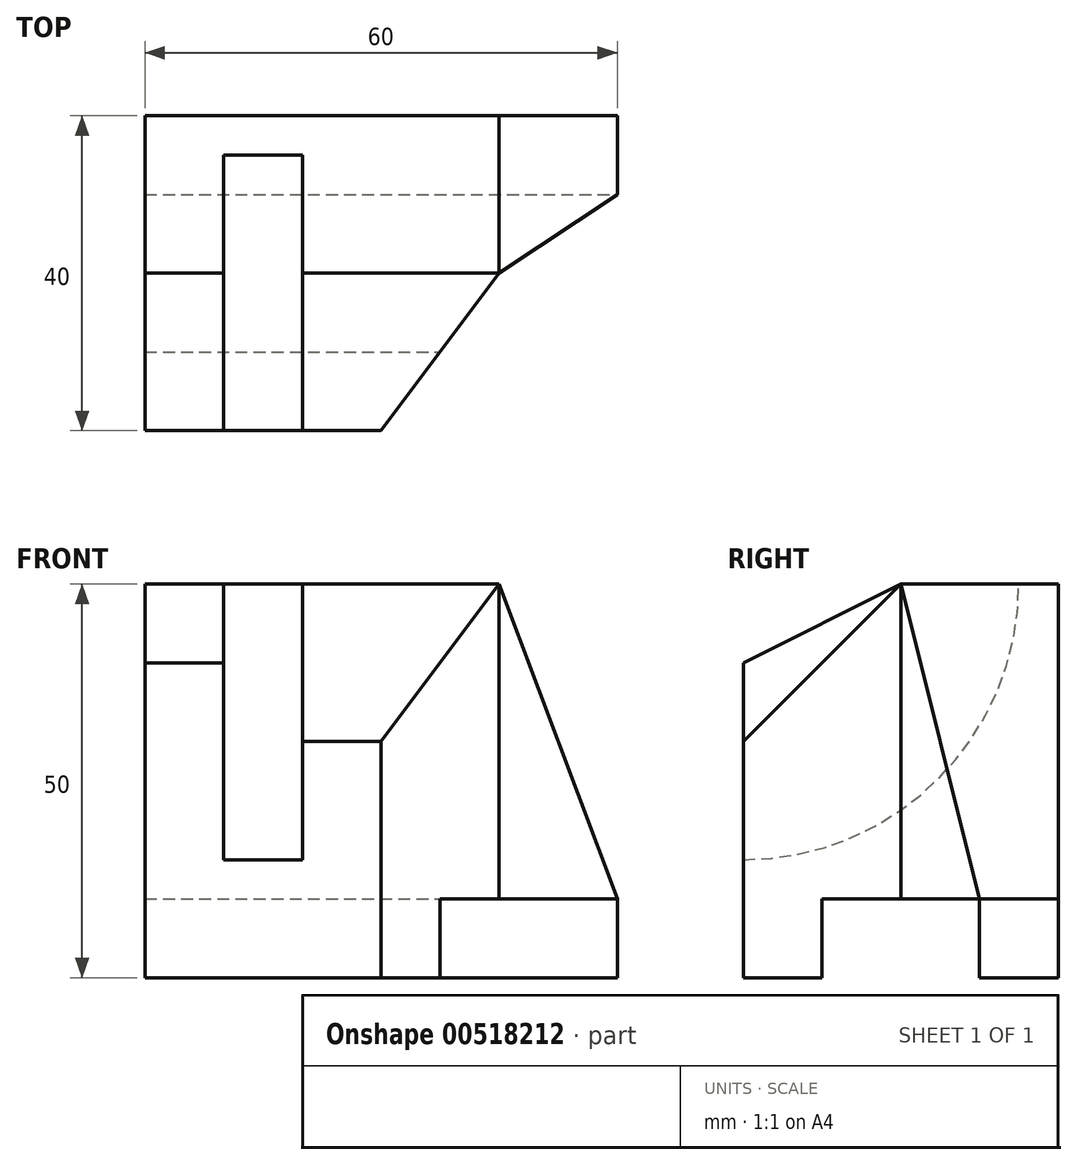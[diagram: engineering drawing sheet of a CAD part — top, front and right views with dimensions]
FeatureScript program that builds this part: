
annotation { "Feature Type Name" : "Feature", "Feature Type Description" : "" }
export const myFeature = defineFeature(function(context is Context, id is Id, definition is map)
    precondition{}
    {
        {
            var Q0;
            Q0=qCreatedBy(makeId("Top.planeOp"),FACE);
            var sketch = newSketch(context, id + "F0", { "sketchPlane" : qUnion([Q0])});
            skLineSegment(sketch, "E0.bottom", {"start": v(0, 0) * mm, "end": v(60, 0) * mm});
            skLineSegment(sketch, "E0.top", {"start": v(0, 40) * mm, "end": v(60, 40) * mm});
            skLineSegment(sketch, "E0.left", {"start": v(0, 0) * mm, "end": v(0, 40) * mm});
            skLineSegment(sketch, "E0.right", {"start": v(60, 0) * mm, "end": v(60, 40) * mm});
            skSolve(sketch);
        }
        {
            var Q0;
            Q0=makeQuery(id+"F0.imprint","IMPRINT",FACE,{"disambiguationData":[TD([[makeQuery(id+"F0.imprint","IMPRINT",EDGE,{"derivedFrom":sQuery(id+"F0.wireOp",EDGE,"E0.bottom")}),1.0]])]});
            extrude(context, id + "F1", {"entities" : qUnion([Q0]), "depth" : 50 * mm, "offsetDistance" : 25 * mm});
        }
        {
            var Q0;
            Q0=makeQuery(id+"F1.opExtrude","CAP_FACE",FACE,{"disambiguationData":[OSD([sQuery(id+"F0.wireOp",EDGE,"E0.bottom"),sQuery(id+"F0.wireOp",EDGE,"E0.top"),sQuery(id+"F0.wireOp",EDGE,"E0.left"),sQuery(id+"F0.wireOp",EDGE,"E0.right")])],"isStart":false});
            var sketch = newSketch(context, id + "F2", { "sketchPlane" : qUnion([Q0])});
            skLineSegment(sketch, "E1", {"start": v(10, 0) * mm, "end": v(10, 35) * mm});
            skLineSegment(sketch, "E2", {"start": v(10, 35) * mm, "end": v(20, 35) * mm});
            skLineSegment(sketch, "E3", {"start": v(20, 35) * mm, "end": v(20, 0) * mm});
            skSolve(sketch);
        }
        {
            var Q0;
            {var subQ0=sQuery(id+"F2.wireOp",EDGE,"E1");Q0=makeQuery(id+"F2.imprint","IMPRINT",FACE,{"disambiguationData":[TD([[makeQuery(id+"F2.imprint","IMPRINT",EDGE,{"derivedFrom":subQ0}),-1.0]])]});}
            extrude(context, id + "F3", {"entities" : qUnion([Q0]), "operationType" : NewBodyOperationType.REMOVE, "oppositeDirection" : true, "depth" : 35 * mm, "offsetDistance" : 25 * mm});
        }
        {
            var Q0;
            Q0=makeQuery(id+"F3.boolean.opBoolean","COPY",EDGE,{"derivedFrom":makeQuery(id+"F3.opExtrude","CAP_EDGE",EDGE,{"disambiguationData":[OSD([sQuery(id+"F2.wireOp",EDGE,"E2")])],"isStart":false})});
            fillet(context, id + "F4", {"entities" : qUnion([Q0]), "radius" : 35 * mm, "tangentPropagation" : true, "allowEdgeOverflow" : false});
        }
        {
            var Q0;
            Q0=makeQuery(id+"F1.opExtrude","SWEPT_FACE",FACE,{"disambiguationData":[OSD([sQuery(id+"F0.wireOp",EDGE,"E0.right")])]});
            var sketch = newSketch(context, id + "F5", { "sketchPlane" : qUnion([Q0])});
            skLineSegment(sketch, "E4", {"start": v(10, 0) * mm, "end": v(10, 10) * mm});
            skLineSegment(sketch, "E5", {"start": v(10, 10) * mm, "end": v(30, 10) * mm});
            skLineSegment(sketch, "E6", {"start": v(30, 10) * mm, "end": v(30, 0) * mm});
            skSolve(sketch);
        }
        {
            var Q0;
            {var subQ0=sQuery(id+"F5.wireOp",EDGE,"E4");Q0=makeQuery(id+"F5.imprint","IMPRINT",FACE,{"disambiguationData":[TD([[makeQuery(id+"F5.imprint","IMPRINT",EDGE,{"derivedFrom":subQ0}),-1.0]])]});}
            extrude(context, id + "F6", {"entities" : qUnion([Q0]), "operationType" : NewBodyOperationType.REMOVE, "endBound" : BoundingType.THROUGH_ALL, "oppositeDirection" : true, "depth" : 25 * mm, "offsetDistance" : 25 * mm});
        }
        {
            var Q0;
            Q0=makeQuery(id+"F1.opExtrude","CAP_FACE",FACE,{"disambiguationData":[OSD([sQuery(id+"F0.wireOp",EDGE,"E0.bottom"),sQuery(id+"F0.wireOp",EDGE,"E0.top"),sQuery(id+"F0.wireOp",EDGE,"E0.left"),sQuery(id+"F0.wireOp",EDGE,"E0.right")])],"isStart":false});
            var sketch = newSketch(context, id + "F7", { "sketchPlane" : qUnion([Q0])});
            skLineSegment(sketch, "E7", {"start": v(60, 20) * mm, "end": v(20, 20) * mm});
            skLineSegment(sketch, "E8", {"start": v(45, 40) * mm, "end": v(45, 20) * mm});
            skLineSegment(sketch, "E9", {"start": v(20, 30) * mm, "end": v(60, 30) * mm});
            skLineSegment(sketch, "E10", {"start": v(60, 30) * mm, "end": v(45, 20) * mm});
            skSolve(sketch);
        }
        {
            var Q0;
            {var subQ3=sQuery(id+"F7.wireOp",EDGE,"E10");Q0=makeQuery(id+"F7.imprint","IMPRINT",FACE,{"disambiguationData":[TD([[makeQuery(id+"F7.imprint","IMPRINT",EDGE,{"derivedFrom":subQ3}),1.0]])]});}
            extrude(context, id + "F8", {"entities" : qUnion([Q0]), "operationType" : NewBodyOperationType.REMOVE, "endBound" : BoundingType.THROUGH_ALL, "oppositeDirection" : true, "depth" : 25 * mm, "offsetDistance" : 25 * mm});
        }
        {
            var Q0;
            Q0=makeQuery(id+"F1.opExtrude","CAP_FACE",FACE,{"disambiguationData":[OSD([sQuery(id+"F0.wireOp",EDGE,"E0.bottom"),sQuery(id+"F0.wireOp",EDGE,"E0.top"),sQuery(id+"F0.wireOp",EDGE,"E0.left"),sQuery(id+"F0.wireOp",EDGE,"E0.right")])],"isStart":false});
            var sketch = newSketch(context, id + "F9", { "sketchPlane" : qUnion([Q0])});
            skLineSegment(sketch, "E11", {"start": v(45, 20) * mm, "end": v(30, 0) * mm});
            skSolve(sketch);
        }
        {
            var Q0;
            {var subQ0=sQuery(id+"F9.wireOp",EDGE,"E11");Q0=makeQuery(id+"F9.imprint","IMPRINT",FACE,{"disambiguationData":[TD([[makeQuery(id+"F9.imprint","IMPRINT",EDGE,{"derivedFrom":subQ0}),1.0]])]});}
            extrude(context, id + "F10", {"entities" : qUnion([Q0]), "operationType" : NewBodyOperationType.REMOVE, "endBound" : BoundingType.THROUGH_ALL, "oppositeDirection" : true, "depth" : 25 * mm, "offsetDistance" : 25 * mm});
        }
        {
            var Q0;
            Q0=makeQuery(id+"F1.opExtrude","CAP_FACE",FACE,{"disambiguationData":[OSD([sQuery(id+"F0.wireOp",EDGE,"E0.bottom"),sQuery(id+"F0.wireOp",EDGE,"E0.top"),sQuery(id+"F0.wireOp",EDGE,"E0.left"),sQuery(id+"F0.wireOp",EDGE,"E0.right")])],"isStart":false});
            var sketch = newSketch(context, id + "F11", { "sketchPlane" : qUnion([Q0])});
            skLineSegment(sketch, "E12", {"start": v(45, 20) * mm, "end": v(45, 40) * mm});
            skSolve(sketch);
        }
        {
            var Q0;
            Q0=makeQuery(id+"F1.opExtrude","SWEPT_FACE",FACE,{"disambiguationData":[OSD([sQuery(id+"F0.wireOp",EDGE,"E0.top")])]});
            var sketch = newSketch(context, id + "F12", { "sketchPlane" : qUnion([Q0])});
            skLineSegment(sketch, "E13", {"start": v(-45, 50) * mm, "end": v(-60, 10) * mm});
            skSolve(sketch);
        }
        {
            var Q0;
            {var subQ0=sQuery(id+"F11.wireOp",EDGE,"E12");Q0=makeQuery(id+"F11.imprint","IMPRINT",FACE,{"disambiguationData":[TD([[makeQuery(id+"F11.imprint","IMPRINT",EDGE,{"derivedFrom":subQ0}),-1.0]])]});}
            var Q1;
            Q1=sQuery(id+"F12.wireOp",EDGE,"E13");
            sweep(context, id + "F13", {"operationType" : NewBodyOperationType.REMOVE, "profiles" : qUnion([Q0]), "path" : qUnion([Q1])});
        }
        {
            var Q0;
            Q0=makeQuery(id+"F1.opExtrude","CAP_FACE",FACE,{"disambiguationData":[OSD([sQuery(id+"F0.wireOp",EDGE,"E0.bottom"),sQuery(id+"F0.wireOp",EDGE,"E0.top"),sQuery(id+"F0.wireOp",EDGE,"E0.left"),sQuery(id+"F0.wireOp",EDGE,"E0.right")])],"isStart":false});
            var sketch = newSketch(context, id + "F14", { "sketchPlane" : qUnion([Q0])});
            skLineSegment(sketch, "E14", {"start": v(45, 20) * mm, "end": v(20, 20) * mm});
            skSolve(sketch);
        }
        {
            var Q0;
            Q0=makeQuery(id+"F3.boolean.opBoolean","COPY",FACE,{"derivedFrom":makeQuery(id+"F3.opExtrude","SWEPT_FACE",FACE,{"disambiguationData":[OSD([sQuery(id+"F2.wireOp",EDGE,"E3")])]})});
            var sketch = newSketch(context, id + "F15", { "sketchPlane" : qUnion([Q0])});
            skLineSegment(sketch, "E15", {"start": v(-20, 50) * mm, "end": v(0, 30) * mm});
            skSolve(sketch);
        }
        {
            var Q0;
            {var subQ0=sQuery(id+"F14.wireOp",EDGE,"E14");Q0=makeQuery(id+"F14.imprint","IMPRINT",FACE,{"disambiguationData":[TD([[makeQuery(id+"F14.imprint","IMPRINT",EDGE,{"derivedFrom":subQ0}),1.0]])]});}
            var Q1;
            Q1=sQuery(id+"F15.wireOp",EDGE,"E15");
            sweep(context, id + "F16", {"operationType" : NewBodyOperationType.REMOVE, "profiles" : qUnion([Q0]), "path" : qUnion([Q1])});
        }
        {
            var Q0;
            Q0=makeQuery(id+"F1.opExtrude","CAP_FACE",FACE,{"disambiguationData":[OSD([sQuery(id+"F0.wireOp",EDGE,"E0.bottom"),sQuery(id+"F0.wireOp",EDGE,"E0.top"),sQuery(id+"F0.wireOp",EDGE,"E0.left"),sQuery(id+"F0.wireOp",EDGE,"E0.right")])],"isStart":false});
            var sketch = newSketch(context, id + "F17", { "sketchPlane" : qUnion([Q0])});
            skLineSegment(sketch, "E16", {"start": v(10, 20) * mm, "end": v(0, 20) * mm});
            skSolve(sketch);
        }
        {
            var Q0;
            Q0=makeQuery(id+"F1.opExtrude","SWEPT_FACE",FACE,{"disambiguationData":[OSD([sQuery(id+"F0.wireOp",EDGE,"E0.left")])]});
            var sketch = newSketch(context, id + "F18", { "sketchPlane" : qUnion([Q0])});
            skLineSegment(sketch, "E17", {"start": v(-20, 50) * mm, "end": v(0, 40) * mm});
            skSolve(sketch);
        }
        {
            var Q0;
            {var subQ0=sQuery(id+"F17.wireOp",EDGE,"E16");Q0=makeQuery(id+"F17.imprint","IMPRINT",FACE,{"disambiguationData":[TD([[makeQuery(id+"F17.imprint","IMPRINT",EDGE,{"derivedFrom":subQ0}),1.0]])]});}
            var Q1;
            Q1=sQuery(id+"F18.wireOp",EDGE,"E17");
            sweep(context, id + "F19", {"operationType" : NewBodyOperationType.REMOVE, "profiles" : qUnion([Q0]), "path" : qUnion([Q1])});
        }
    });
